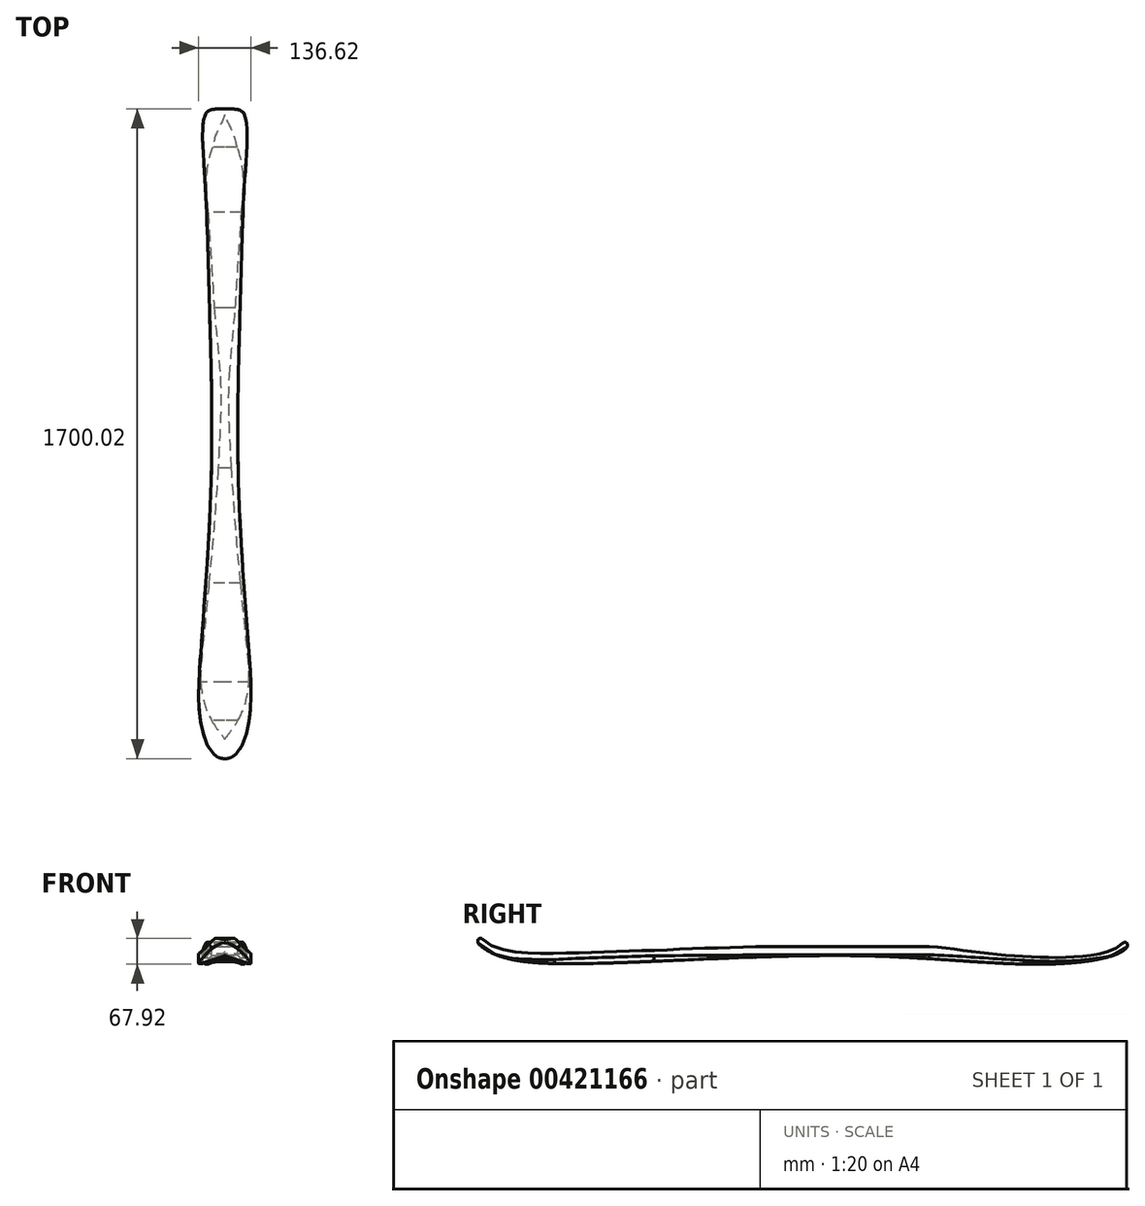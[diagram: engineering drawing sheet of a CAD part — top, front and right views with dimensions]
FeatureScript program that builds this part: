
annotation { "Feature Type Name" : "Feature", "Feature Type Description" : "" }
export const myFeature = defineFeature(function(context is Context, id is Id, definition is map)
    precondition{}
    {
        {
            var Q0;
            Q0=qCreatedBy(makeId("Right.planeOp"),FACE);
            var sketch = newSketch(context, id + "F0", { "sketchPlane" : qUnion([Q0])});
            skLineSegment(sketch, "E0.bottom", {"start": v(-1000, 0) * mm, "end": v(700, 0) * mm, "construction": true});
            skLineSegment(sketch, "E0.top", {"start": v(-1000, -45) * mm, "end": v(700, -45) * mm, "construction": true});
            skLineSegment(sketch, "E0.left", {"start": v(-1000, 0) * mm, "end": v(-1000, -45) * mm, "construction": true});
            skLineSegment(sketch, "E0.right", {"start": v(700, 0) * mm, "end": v(700, -45) * mm, "construction": true});
            skPoint(sketch, "E1.3.internal.snap0", {"position": v(-1000, -22.5) * mm});
            skFitSpline(sketch, "E1", {"points": [v(-1000, 10) * mm, v(-950, -22.5) * mm, v(-760, -45) * mm, v(0, -24) * mm, v(520, -45) * mm, v(700, 0) * mm], "startDerivative": vector(249.3, -384.63) * mm, "endDerivative": vector(259.11, 471.11) * mm});
            skLineSegment(sketch, "E2", {"start": v(-240, 0) * mm, "end": v(180, 0) * mm});
            skArc(sketch, "E3", {"start": v(-988.18, 19.15) * mm, "mid": v(-998.3, 20.01) * mm, "end": v(-1000, 10) * mm});
            skFitSpline(sketch, "E4", {"points": [v(-988.18, 19.15) * mm, v(-760, -17) * mm, v(-520, -9) * mm, v(-240, 0) * mm], "startDerivative": vector(357.43, -389.9) * mm, "endDerivative": vector(510.1, 0) * mm});
            skArc(sketch, "E5", {"start": v(700, 0) * mm, "mid": v(697.77, 9.73) * mm, "end": v(687.85, 8.63) * mm});
            skFitSpline(sketch, "E6", {"points": [v(180, 0) * mm, v(247.5, -6.88) * mm, v(520, -28.75) * mm, v(687.85, 8.63) * mm], "startDerivative": vector(344.95, 0) * mm, "endDerivative": vector(198.08, 220) * mm});
            skSolve(sketch);
        }
        {
            var Q0;
            Q0=qCreatedBy(makeId("Top.planeOp"),FACE);
            var sketch = newSketch(context, id + "F1", { "sketchPlane" : qUnion([Q0])});
            skFitSpline(sketch, "E7", {"points": [v(0, 700) * mm, v(-50, 687.85) * mm, v(-52.5, 520) * mm, v(-40, 180) * mm, v(-35, -240) * mm, v(-60, -680) * mm, v(-60, -920) * mm, v(0, -1000) * mm], "startDerivative": vector(-1236.08, 0) * mm, "endDerivative": vector(1045, 0) * mm});
            skLineSegment(sketch, "E8", {"start": v(0, 700) * mm, "end": v(0, -1000) * mm, "construction": true});
            skFitSpline(sketch, "E9.MirrorCS", {"points": [v(0, 700) * mm, v(50, 687.85) * mm, v(52.5, 520) * mm, v(40, 180) * mm, v(35, -240) * mm, v(60, -680) * mm, v(60, -920) * mm, v(0, -1000) * mm], "startDerivative": vector(1236.08, 0) * mm, "endDerivative": vector(-1045, 0) * mm});
            skLineSegment(sketch, "E10.bottom", {"start": v(-75, 750) * mm, "end": v(75, 750) * mm});
            skLineSegment(sketch, "E10.top", {"start": v(-75, -1050) * mm, "end": v(75, -1050) * mm});
            skLineSegment(sketch, "E10.left", {"start": v(-75, 750) * mm, "end": v(-75, -1050) * mm});
            skLineSegment(sketch, "E10.right", {"start": v(75, 750) * mm, "end": v(75, -1050) * mm});
            skSolve(sketch);
        }
        {
            var Q0;
            Q0=makeQuery(id+"F0.imprint","IMPRINT",FACE,{"disambiguationData":[TD([[makeQuery(id+"F0.imprint","IMPRINT",EDGE,{"derivedFrom":sQuery(id+"F0.wireOp",EDGE,"E1")}),1.0]])]});
            extrude(context, id + "F2", {"entities" : qUnion([Q0]), "endBound" : BoundingType.SYMMETRIC, "depth" : 140 * mm});
        }
        {
            var Q0;
            Q0=makeQuery(id+"F1.imprint","IMPRINT",FACE,{"disambiguationData":[TD([[makeQuery(id+"F1.imprint","IMPRINT",EDGE,{"derivedFrom":sQuery(id+"F1.wireOp",EDGE,"E7")}),-1.0]])]});
            extrude(context, id + "F3", {"entities" : qUnion([Q0]), "operationType" : NewBodyOperationType.REMOVE, "endBound" : BoundingType.SYMMETRIC, "depth" : 100 * mm});
        }
        {
            var Q0;
            Q0=qCreatedBy(makeId("Front.planeOp"),FACE);
            cPlane(context, id + "F4", {"entities" : qUnion([Q0]), "cplaneType" : CPlaneType.OFFSET, "offset" : 240 * mm, "width" : 150 * mm, "height" : 150 * mm});
        }
        {
            var Q0;
            Q0=qCreatedBy(id+"F4.planeOp",FACE);
            cPlane(context, id + "F5", {"entities" : qUnion([Q0]), "cplaneType" : CPlaneType.OFFSET, "offset" : 300 * mm, "width" : 150 * mm, "height" : 150 * mm});
        }
        {
            var Q0;
            Q0=qCreatedBy(id+"F5.planeOp",FACE);
            cPlane(context, id + "F6", {"entities" : qUnion([Q0]), "cplaneType" : CPlaneType.OFFSET, "offset" : 260 * mm, "width" : 150 * mm, "height" : 150 * mm});
        }
        {
            var Q0;
            Q0=qCreatedBy(id+"F6.planeOp",FACE);
            cPlane(context, id + "F7", {"entities" : qUnion([Q0]), "cplaneType" : CPlaneType.OFFSET, "offset" : 100 * mm, "width" : 150 * mm, "height" : 150 * mm});
        }
        {
            var Q0;
            Q0=qCreatedBy(makeId("Front.planeOp"),FACE);
            cPlane(context, id + "F8", {"entities" : qUnion([Q0]), "cplaneType" : CPlaneType.OFFSET, "offset" : 180 * mm, "oppositeDirection" : true, "width" : 150 * mm, "height" : 150 * mm});
        }
        {
            var Q0;
            Q0=qCreatedBy(id+"F8.planeOp",FACE);
            cPlane(context, id + "F9", {"entities" : qUnion([Q0]), "cplaneType" : CPlaneType.OFFSET, "offset" : 250 * mm, "oppositeDirection" : true, "width" : 150 * mm, "height" : 150 * mm});
        }
        {
            var Q0;
            Q0=qCreatedBy(id+"F9.planeOp",FACE);
            cPlane(context, id + "F10", {"entities" : qUnion([Q0]), "cplaneType" : CPlaneType.OFFSET, "offset" : 170 * mm, "oppositeDirection" : true, "width" : 150 * mm, "height" : 150 * mm});
        }
        {
            var Q0;
            Q0=qCreatedBy(id+"F10.planeOp",FACE);
            cPlane(context, id + "F11", {"entities" : qUnion([Q0]), "cplaneType" : CPlaneType.OFFSET, "offset" : 85 * mm, "oppositeDirection" : true, "width" : 150 * mm, "height" : 150 * mm});
        }
        {
            var Q0;
            Q0=qCreatedBy(id+"F7.planeOp",FACE);
            cPlane(context, id + "F12", {"entities" : qUnion([Q0]), "cplaneType" : CPlaneType.OFFSET, "offset" : 50 * mm, "width" : 150 * mm, "height" : 150 * mm});
        }
        {
            var Q0;
            Q0=qCreatedBy(makeId("Top.planeOp"),FACE);
            cPlane(context, id + "F13", {"entities" : qUnion([Q0]), "cplaneType" : CPlaneType.OFFSET, "offset" : 46 * mm, "oppositeDirection" : true, "width" : 150 * mm, "height" : 150 * mm});
        }
        {
            var Q0;
            Q0=qCreatedBy(makeId("Right.planeOp"),FACE);
            var sketch = newSketch(context, id + "F14", { "sketchPlane" : qUnion([Q0])});
            skFitSpline(sketch, "E11", {"points": [v(-950, -22.5) * mm, v(-900, -32.05) * mm, v(-800, -34.02) * mm, v(-760, -32) * mm, v(-540, -24.26) * mm, v(-520, -24) * mm, v(-240, -22) * mm, v(0, -22) * mm, v(180, -22) * mm, v(247.5, -24.88) * mm, v(430, -36.26) * mm, v(520, -38.75) * mm, v(600, -33.38) * mm, v(685, -13.47) * mm], "startDerivative": vector(812.8, -310.38) * mm, "endDerivative": vector(960.2, 551.45) * mm});
            skPoint(sketch, "E12", {"position": v(-900, -14.55) * mm});
            skPoint(sketch, "E13", {"position": v(-800, -18.02) * mm});
            skPoint(sketch, "E14", {"position": v(-540, -9.76) * mm});
            skPoint(sketch, "E15", {"position": v(430, -26.26) * mm});
            skPoint(sketch, "E16", {"position": v(600, -23.38) * mm});
            skLineSegment(sketch, "E17", {"start": v(663.32, -25.92) * mm, "end": v(685, -13.47) * mm, "construction": true});
            skLineSegment(sketch, "E18", {"start": v(-900, -32.05) * mm, "end": v(-900, -32.05) * mm});
            skLineSegment(sketch, "E19", {"start": v(-800, -34.02) * mm, "end": v(-800, -39.05) * mm, "construction": true});
            skLineSegment(sketch, "E20", {"start": v(-540, -24.26) * mm, "end": v(-540, -31.48) * mm, "construction": true});
            skLineSegment(sketch, "E21", {"start": v(-900, -32.05) * mm, "end": v(-900, -35.35) * mm, "construction": true});
            skLineSegment(sketch, "E22", {"start": v(-240, -22) * mm, "end": v(-240, -31.61) * mm, "construction": true});
            skLineSegment(sketch, "E23", {"start": v(0, -22) * mm, "end": v(0, -22) * mm});
            skLineSegment(sketch, "E24", {"start": v(180, -22) * mm, "end": v(180, -38.86) * mm, "construction": true});
            skLineSegment(sketch, "E25", {"start": v(430, -36.26) * mm, "end": v(430, -46.86) * mm, "construction": true});
            skLineSegment(sketch, "E26", {"start": v(600, -33.38) * mm, "end": v(600, -44.7) * mm, "construction": true});
            skLineSegment(sketch, "E27", {"start": v(0, -22) * mm, "end": v(0, -33.93) * mm, "construction": true});
            skSolve(sketch);
        }
        {
            var Q0;
            Q0=qCreatedBy(id+"F13.planeOp",FACE);
            var sketch = newSketch(context, id + "F15", { "sketchPlane" : qUnion([Q0])});
            skFitSpline(sketch, "E28", {"points": [v(0, 700) * mm, v(-50, 687.85) * mm, v(-52.5, 520) * mm, v(-40, 180) * mm, v(-35, -240) * mm, v(-60, -680) * mm, v(-60, -920) * mm, v(0, -1000) * mm], "startDerivative": vector(-1236.08, 0) * mm, "endDerivative": vector(1045, 0) * mm});
            skLineSegment(sketch, "E29", {"start": v(0, 700) * mm, "end": v(0, -1000) * mm, "construction": true});
            skFitSpline(sketch, "E30.MirrorCS", {"points": [v(0, 700) * mm, v(50, 687.85) * mm, v(52.5, 520) * mm, v(40, 180) * mm, v(35, -240) * mm, v(60, -680) * mm, v(60, -920) * mm, v(0, -1000) * mm], "startDerivative": vector(1236.08, 0) * mm, "endDerivative": vector(-1045, 0) * mm});
            skLineSegment(sketch, "E31.bottom", {"start": v(-75, 750) * mm, "end": v(75, 750) * mm});
            skLineSegment(sketch, "E31.top", {"start": v(-75, -1050) * mm, "end": v(75, -1050) * mm});
            skLineSegment(sketch, "E31.left", {"start": v(-75, 750) * mm, "end": v(-75, -1050) * mm});
            skLineSegment(sketch, "E31.right", {"start": v(75, 750) * mm, "end": v(75, -1050) * mm});
            skPoint(sketch, "E32", {"position": v(51.58, -950) * mm});
            skPoint(sketch, "E33", {"position": v(-51.58, -950) * mm});
            skPoint(sketch, "E34", {"position": v(63.62, -900) * mm});
            skPoint(sketch, "E35", {"position": v(-63.62, -900) * mm});
            skPoint(sketch, "E36", {"position": v(-67.82, -800) * mm});
            skPoint(sketch, "E37", {"position": v(67.82, -800) * mm});
            skPoint(sketch, "E38", {"position": v(-49.6, -540) * mm});
            skPoint(sketch, "E39", {"position": v(49.6, -540) * mm});
            skPoint(sketch, "E40", {"position": v(-35.38, 0) * mm});
            skPoint(sketch, "E41", {"position": v(35.38, 0) * mm});
            skPoint(sketch, "E42", {"position": v(-47.76, 430) * mm});
            skPoint(sketch, "E43", {"position": v(47.76, 430) * mm});
            skPoint(sketch, "E44", {"position": v(-57.53, 600) * mm});
            skPoint(sketch, "E45", {"position": v(57.53, 600) * mm});
            skPoint(sketch, "E46", {"position": v(-51.5, 685) * mm});
            skPoint(sketch, "E47", {"position": v(51.5, 685) * mm});
            skSolve(sketch);
        }
        {
            var Q0;
            Q0=qCreatedBy(id+"F12.planeOp",FACE);
            var sketch = newSketch(context, id + "F16", { "sketchPlane" : qUnion([Q0])});
            skArc(sketch, "E48", {"start": v(51.58, -46) * mm, "mid": v(0, -22.5) * mm, "end": v(-51.58, -46) * mm});
            skLineSegment(sketch, "E49", {"start": v(-51.58, -46) * mm, "end": v(51.58, -46) * mm});
            skPoint(sketch, "E50", {"position": v(0, -22.5) * mm});
            skSolve(sketch);
        }
        {
            var Q0;
            Q0=qCreatedBy(id+"F7.planeOp",FACE);
            var sketch = newSketch(context, id + "F17", { "sketchPlane" : qUnion([Q0])});
            skLineSegment(sketch, "E51", {"start": v(-63.62, -46) * mm, "end": v(63.62, -46) * mm});
            skArc(sketch, "E52", {"start": v(63.62, -46) * mm, "mid": v(0, -32.05) * mm, "end": v(-63.62, -46) * mm});
            skSolve(sketch);
        }
        {
            var Q0;
            Q0=qCreatedBy(id+"F6.planeOp",FACE);
            var sketch = newSketch(context, id + "F18", { "sketchPlane" : qUnion([Q0])});
            skLineSegment(sketch, "E53", {"start": v(-67.82, -46) * mm, "end": v(67.82, -46) * mm});
            skArc(sketch, "E54", {"start": v(67.82, -46) * mm, "mid": v(0, -34.02) * mm, "end": v(-67.82, -46) * mm});
            skSolve(sketch);
        }
        {
            var Q0;
            Q0=qCreatedBy(id+"F5.planeOp",FACE);
            var sketch = newSketch(context, id + "F19", { "sketchPlane" : qUnion([Q0])});
            skArc(sketch, "E55", {"start": v(49.6, -46) * mm, "mid": v(0, -24.26) * mm, "end": v(-49.6, -46) * mm});
            skLineSegment(sketch, "E56", {"start": v(-49.6, -46) * mm, "end": v(49.6, -46) * mm});
            skSolve(sketch);
        }
        {
            var Q0;
            Q0=qCreatedBy(id+"F4.planeOp",FACE);
            var sketch = newSketch(context, id + "F20", { "sketchPlane" : qUnion([Q0])});
            skArc(sketch, "E57", {"start": v(35, -46) * mm, "mid": v(0, -22) * mm, "end": v(-35, -46) * mm});
            skLineSegment(sketch, "E58", {"start": v(-35, -46) * mm, "end": v(35, -46) * mm});
            skSolve(sketch);
        }
        {
            var Q0;
            Q0=qCreatedBy(makeId("Front.planeOp"),FACE);
            var sketch = newSketch(context, id + "F21", { "sketchPlane" : qUnion([Q0])});
            skArc(sketch, "E59", {"start": v(35.38, -46) * mm, "mid": v(0, -22) * mm, "end": v(-35.38, -46) * mm});
            skLineSegment(sketch, "E60", {"start": v(-35.38, -46) * mm, "end": v(35.38, -46) * mm});
            skSolve(sketch);
        }
        {
            var Q0;
            Q0=qCreatedBy(id+"F8.planeOp",FACE);
            var sketch = newSketch(context, id + "F22", { "sketchPlane" : qUnion([Q0])});
            skArc(sketch, "E61", {"start": v(40, -46) * mm, "mid": v(0, -22) * mm, "end": v(-40, -46) * mm});
            skLineSegment(sketch, "E62", {"start": v(-40, -46) * mm, "end": v(40, -46) * mm});
            skSolve(sketch);
        }
        {
            var Q0;
            Q0=qCreatedBy(id+"F9.planeOp",FACE);
            var sketch = newSketch(context, id + "F23", { "sketchPlane" : qUnion([Q0])});
            skArc(sketch, "E63", {"start": v(47.76, -48) * mm, "mid": v(0, -36.26) * mm, "end": v(-47.76, -48) * mm});
            skLineSegment(sketch, "E64", {"start": v(-47.76, -48) * mm, "end": v(47.76, -48) * mm});
            skSolve(sketch);
        }
        {
            var Q0;
            Q0=qCreatedBy(id+"F10.planeOp",FACE);
            var sketch = newSketch(context, id + "F24", { "sketchPlane" : qUnion([Q0])});
            skArc(sketch, "E65", {"start": v(57.53, -46) * mm, "mid": v(0, -33.38) * mm, "end": v(-57.53, -46) * mm});
            skLineSegment(sketch, "E66", {"start": v(-57.53, -46) * mm, "end": v(57.53, -46) * mm});
            skSolve(sketch);
        }
        {
            var Q0;
            Q0=qCreatedBy(id+"F11.planeOp",FACE);
            var sketch = newSketch(context, id + "F25", { "sketchPlane" : qUnion([Q0])});
            skArc(sketch, "E67", {"start": v(51.5, -46) * mm, "mid": v(0, -13.47) * mm, "end": v(-51.5, -46) * mm});
            skLineSegment(sketch, "E68", {"start": v(-51.5, -46) * mm, "end": v(51.5, -46) * mm});
            skSolve(sketch);
        }
        {
            var Q1;
            Q1=makeQuery(id+"F16.imprint","IMPRINT",FACE,{"disambiguationData":[TD([[makeQuery(id+"F16.imprint","IMPRINT",EDGE,{"derivedFrom":sQuery(id+"F16.wireOp",EDGE,"E48")}),1.0]])]});
            var Q2;
            Q2=makeQuery(id+"F17.imprint","IMPRINT",FACE,{"disambiguationData":[TD([[makeQuery(id+"F17.imprint","IMPRINT",EDGE,{"derivedFrom":sQuery(id+"F17.wireOp",EDGE,"E51")}),1.0]])]});
            var Q3;
            Q3=sQuery(id+"F14.wireOp",EDGE,"E11");
            loft(context, id + "F26", {"operationType" : NewBodyOperationType.REMOVE, "addGuides" : true, "sheetProfilesArray" : [{ "sheetProfileEntities" : qUnion([Q1]) }, { "sheetProfileEntities" : qUnion([Q2]) }], "guidesArray" : [{ "guideEntities" : qUnion([Q3]), "guideDerivativeType" : LoftGuideDerivativeType.DEFAULT, "guideDerivativeMagnitude" : 1 }]});
        }
        {
            var Q1;
            Q1=makeQuery(id+"F17.imprint","IMPRINT",FACE,{"disambiguationData":[TD([[makeQuery(id+"F17.imprint","IMPRINT",EDGE,{"derivedFrom":sQuery(id+"F17.wireOp",EDGE,"E51")}),1.0]])]});
            var Q2;
            Q2 = qSketchRegion(id + "F18", true);
            var Q3;
            Q3=sQuery(id+"F14.wireOp",EDGE,"E11");
            loft(context, id + "F27", {"operationType" : NewBodyOperationType.REMOVE, "addGuides" : true, "sheetProfilesArray" : [{ "sheetProfileEntities" : qUnion([Q1]) }, { "sheetProfileEntities" : qUnion([Q2]) }], "guidesArray" : [{ "guideEntities" : qUnion([Q3]), "guideDerivativeType" : LoftGuideDerivativeType.DEFAULT, "guideDerivativeMagnitude" : 1 }]});
        }
        {
            var Q1;
            Q1 = qSketchRegion(id + "F18", true);
            var Q2;
            Q2 = qSketchRegion(id + "F19", true);
            var Q3;
            Q3=sQuery(id+"F14.wireOp",EDGE,"E11");
            loft(context, id + "F28", {"operationType" : NewBodyOperationType.REMOVE, "addGuides" : true, "sheetProfilesArray" : [{ "sheetProfileEntities" : qUnion([Q1]) }, { "sheetProfileEntities" : qUnion([Q2]) }], "guidesArray" : [{ "guideEntities" : qUnion([Q3]), "guideDerivativeType" : LoftGuideDerivativeType.DEFAULT, "guideDerivativeMagnitude" : 1 }]});
        }
        {
            var Q1;
            Q1 = qSketchRegion(id + "F19", true);
            var Q2;
            Q2 = qSketchRegion(id + "F20", true);
            var Q3;
            Q3=sQuery(id+"F14.wireOp",EDGE,"E11");
            loft(context, id + "F29", {"operationType" : NewBodyOperationType.REMOVE, "addGuides" : true, "sheetProfilesArray" : [{ "sheetProfileEntities" : qUnion([Q1]) }, { "sheetProfileEntities" : qUnion([Q2]) }], "guidesArray" : [{ "guideEntities" : qUnion([Q3]), "guideDerivativeType" : LoftGuideDerivativeType.DEFAULT, "guideDerivativeMagnitude" : 1 }]});
        }
        {
            var Q1;
            Q1 = qSketchRegion(id + "F20", true);
            var Q2;
            Q2 = qSketchRegion(id + "F21", true);
            var Q3;
            Q3=sQuery(id+"F14.wireOp",EDGE,"E11");
            loft(context, id + "F30", {"operationType" : NewBodyOperationType.REMOVE, "addGuides" : true, "sheetProfilesArray" : [{ "sheetProfileEntities" : qUnion([Q1]) }, { "sheetProfileEntities" : qUnion([Q2]) }], "guidesArray" : [{ "guideEntities" : qUnion([Q3]), "guideDerivativeType" : LoftGuideDerivativeType.DEFAULT, "guideDerivativeMagnitude" : 1 }]});
        }
        {
            var Q1;
            Q1=makeQuery(id+"F21.imprint","IMPRINT",FACE,{"disambiguationData":[TD([[makeQuery(id+"F21.imprint","IMPRINT",EDGE,{"derivedFrom":sQuery(id+"F21.wireOp",EDGE,"E59")}),1.0]])]});
            var Q2;
            Q2=makeQuery(id+"F22.imprint","IMPRINT",FACE,{"disambiguationData":[TD([[makeQuery(id+"F22.imprint","IMPRINT",EDGE,{"derivedFrom":sQuery(id+"F22.wireOp",EDGE,"E61")}),1.0]])]});
            var Q3;
            Q3=sQuery(id+"F14.wireOp",EDGE,"E11");
            loft(context, id + "F31", {"operationType" : NewBodyOperationType.REMOVE, "addGuides" : true, "sheetProfilesArray" : [{ "sheetProfileEntities" : qUnion([Q1]) }, { "sheetProfileEntities" : qUnion([Q2]) }], "guidesArray" : [{ "guideEntities" : qUnion([Q3]), "guideDerivativeType" : LoftGuideDerivativeType.DEFAULT, "guideDerivativeMagnitude" : 1 }]});
        }
        {
            var Q1;
            Q1=makeQuery(id+"F22.imprint","IMPRINT",FACE,{"disambiguationData":[TD([[makeQuery(id+"F22.imprint","IMPRINT",EDGE,{"derivedFrom":sQuery(id+"F22.wireOp",EDGE,"E61")}),1.0]])]});
            var Q2;
            Q2 = qSketchRegion(id + "F23", true);
            var Q3;
            Q3=sQuery(id+"F14.wireOp",EDGE,"E11");
            loft(context, id + "F32", {"operationType" : NewBodyOperationType.REMOVE, "addGuides" : true, "sheetProfilesArray" : [{ "sheetProfileEntities" : qUnion([Q1]) }, { "sheetProfileEntities" : qUnion([Q2]) }], "guidesArray" : [{ "guideEntities" : qUnion([Q3]), "guideDerivativeType" : LoftGuideDerivativeType.DEFAULT, "guideDerivativeMagnitude" : 1 }]});
        }
        {
            var Q1;
            Q1 = qSketchRegion(id + "F23", true);
            var Q2;
            Q2 = qSketchRegion(id + "F24", true);
            var Q3;
            Q3=sQuery(id+"F14.wireOp",EDGE,"E11");
            loft(context, id + "F33", {"operationType" : NewBodyOperationType.REMOVE, "addGuides" : true, "sheetProfilesArray" : [{ "sheetProfileEntities" : qUnion([Q1]) }, { "sheetProfileEntities" : qUnion([Q2]) }], "guidesArray" : [{ "guideEntities" : qUnion([Q3]), "guideDerivativeType" : LoftGuideDerivativeType.DEFAULT, "guideDerivativeMagnitude" : 1 }]});
        }
        {
            var Q1;
            Q1=makeQuery(id+"F24.imprint","IMPRINT",FACE,{"disambiguationData":[TD([[makeQuery(id+"F24.imprint","IMPRINT",EDGE,{"derivedFrom":sQuery(id+"F24.wireOp",EDGE,"E65")}),1.0]])]});
            var Q2;
            Q2=makeQuery(id+"F25.imprint","IMPRINT",FACE,{"disambiguationData":[TD([[makeQuery(id+"F25.imprint","IMPRINT",EDGE,{"derivedFrom":sQuery(id+"F25.wireOp",EDGE,"E67")}),1.0]])]});
            var Q3;
            Q3=sQuery(id+"F14.wireOp",EDGE,"E11");
            loft(context, id + "F34", {"operationType" : NewBodyOperationType.REMOVE, "addGuides" : true, "sheetProfilesArray" : [{ "sheetProfileEntities" : qUnion([Q1]) }, { "sheetProfileEntities" : qUnion([Q2]) }], "guidesArray" : [{ "guideEntities" : qUnion([Q3]), "guideDerivativeType" : LoftGuideDerivativeType.DEFAULT, "guideDerivativeMagnitude" : 1 }]});
        }
    });
